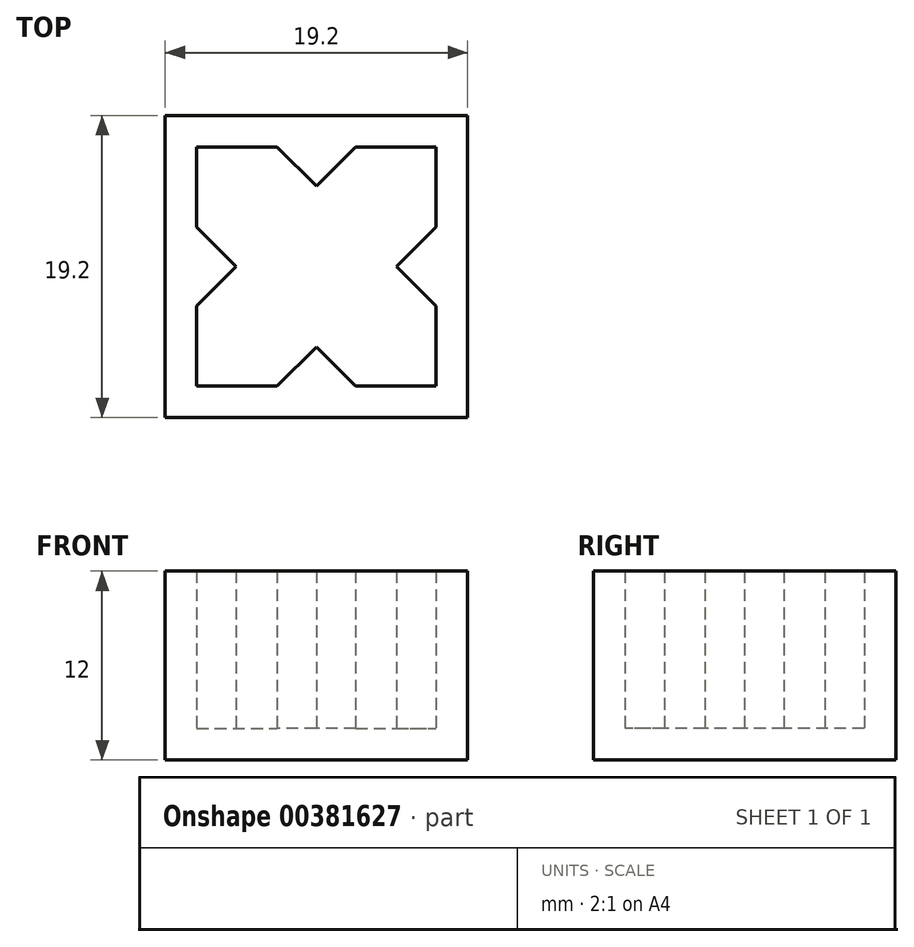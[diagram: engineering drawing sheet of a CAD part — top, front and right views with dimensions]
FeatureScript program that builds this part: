
annotation { "Feature Type Name" : "Feature", "Feature Type Description" : "" }
export const myFeature = defineFeature(function(context is Context, id is Id, definition is map)
    precondition{}
    {
        {
            var Q0;
            Q0=qCreatedBy(makeId("Top.planeOp"),FACE);
            var sketch = newSketch(context, id + "F0", { "sketchPlane" : qUnion([Q0])});
            skLineSegment(sketch, "E0.bottom", {"start": v(-9.64, 10.57) * mm, "end": v(5.56, 10.57) * mm});
            skLineSegment(sketch, "E0.top", {"start": v(-9.64, -4.63) * mm, "end": v(5.56, -4.63) * mm});
            skLineSegment(sketch, "E0.left", {"start": v(-9.64, 10.57) * mm, "end": v(-9.64, -4.63) * mm});
            skLineSegment(sketch, "E0.right", {"start": v(5.56, 10.57) * mm, "end": v(5.56, -4.63) * mm});
            skLineSegment(sketch, "E1", {"start": v(-2.04, 10.57) * mm, "end": v(-2.04, -4.63) * mm, "construction": true});
            skLineSegment(sketch, "E2", {"start": v(-9.64, 2.97) * mm, "end": v(5.56, 2.97) * mm, "construction": true});
            skLineSegment(sketch, "E3", {"start": v(0.46, 10.57) * mm, "end": v(-2.04, 8.07) * mm});
            skLineSegment(sketch, "E4", {"start": v(-2.04, 8.07) * mm, "end": v(-4.54, 10.57) * mm});
            skLineSegment(sketch, "E5.MirrorCS", {"start": v(0.46, -4.63) * mm, "end": v(-2.04, -2.13) * mm});
            skLineSegment(sketch, "E6.MirrorCS", {"start": v(-2.04, -2.13) * mm, "end": v(-4.54, -4.63) * mm});
            skLineSegment(sketch, "E7", {"start": v(-9.64, 5.47) * mm, "end": v(-7.14, 2.97) * mm});
            skLineSegment(sketch, "E8", {"start": v(-7.14, 2.97) * mm, "end": v(-9.64, 0.47) * mm});
            skLineSegment(sketch, "E9.MirrorCS", {"start": v(5.56, 5.47) * mm, "end": v(3.06, 2.97) * mm});
            skLineSegment(sketch, "E10.MirrorCS", {"start": v(3.06, 2.97) * mm, "end": v(5.56, 0.47) * mm});
            skSolve(sketch);
        }
        {
            var Q0;
            {var subQ0=sQuery(id+"F0.wireOp",EDGE,"E3");Q0=makeQuery(id+"F0.imprint","IMPRINT",FACE,{"disambiguationData":[TD([[makeQuery(id+"F0.imprint","IMPRINT",EDGE,{"derivedFrom":subQ0}),1.0]])]});}
            var Q1;
            {var subQ0=sQuery(id+"F0.wireOp",EDGE,"E7");Q1=makeQuery(id+"F0.imprint","IMPRINT",FACE,{"disambiguationData":[TD([[makeQuery(id+"F0.imprint","IMPRINT",EDGE,{"derivedFrom":subQ0}),-1.0]])]});}
            var Q2;
            {var subQ0=sQuery(id+"F0.wireOp",EDGE,"E5.MirrorCS");Q2=makeQuery(id+"F0.imprint","IMPRINT",FACE,{"disambiguationData":[TD([[makeQuery(id+"F0.imprint","IMPRINT",EDGE,{"derivedFrom":subQ0}),1.0]])]});}
            var Q3;
            {var subQ0=sQuery(id+"F0.wireOp",EDGE,"E9.MirrorCS");Q3=makeQuery(id+"F0.imprint","IMPRINT",FACE,{"disambiguationData":[TD([[makeQuery(id+"F0.imprint","IMPRINT",EDGE,{"derivedFrom":subQ0}),1.0]])]});}
            var Q4;
            {var subQ0=sQuery(id+"F0.wireOp",EDGE,"E3");Q4=makeQuery(id+"F0.imprint","IMPRINT",FACE,{"disambiguationData":[TD([[makeQuery(id+"F0.imprint","IMPRINT",EDGE,{"derivedFrom":subQ0}),-1.0]])]});}
            extrude(context, id + "F1", {"entities" : qUnion([Q0, Q1, Q2, Q3, Q4]), "depth" : 10 * mm});
        }
        {
            var Q0;
            Q0=makeQuery(id+"F1.opExtrude","CAP_FACE",FACE,{"disambiguationData":[OSD([sQuery(id+"F0.wireOp",EDGE,"E0.bottom"),sQuery(id+"F0.wireOp",EDGE,"E0.top"),sQuery(id+"F0.wireOp",EDGE,"E0.left"),sQuery(id+"F0.wireOp",EDGE,"E0.right")])],"isStart":false});
            shell(context, id + "F2", {"entities" : qUnion([Q0]), "thickness" : 2 * mm, "oppositeDirection" : true});
        }
        {
            var Q0;
            {var subQ0=sQuery(id+"F0.wireOp",EDGE,"E3");Q0=makeQuery(id+"F0.imprint","IMPRINT",FACE,{"disambiguationData":[TD([[makeQuery(id+"F0.imprint","IMPRINT",EDGE,{"derivedFrom":subQ0}),-1.0]])]});}
            var Q1;
            {var subQ0=sQuery(id+"F0.wireOp",EDGE,"E9.MirrorCS");Q1=makeQuery(id+"F0.imprint","IMPRINT",FACE,{"disambiguationData":[TD([[makeQuery(id+"F0.imprint","IMPRINT",EDGE,{"derivedFrom":subQ0}),1.0]])]});}
            var Q2;
            {var subQ0=sQuery(id+"F0.wireOp",EDGE,"E7");Q2=makeQuery(id+"F0.imprint","IMPRINT",FACE,{"disambiguationData":[TD([[makeQuery(id+"F0.imprint","IMPRINT",EDGE,{"derivedFrom":subQ0}),-1.0]])]});}
            var Q3;
            {var subQ0=sQuery(id+"F0.wireOp",EDGE,"E5.MirrorCS");Q3=makeQuery(id+"F0.imprint","IMPRINT",FACE,{"disambiguationData":[TD([[makeQuery(id+"F0.imprint","IMPRINT",EDGE,{"derivedFrom":subQ0}),1.0]])]});}
            extrude(context, id + "F3", {"entities" : qUnion([Q0, Q1, Q2, Q3]), "operationType" : NewBodyOperationType.ADD, "depth" : 10 * mm});
        }
    });
